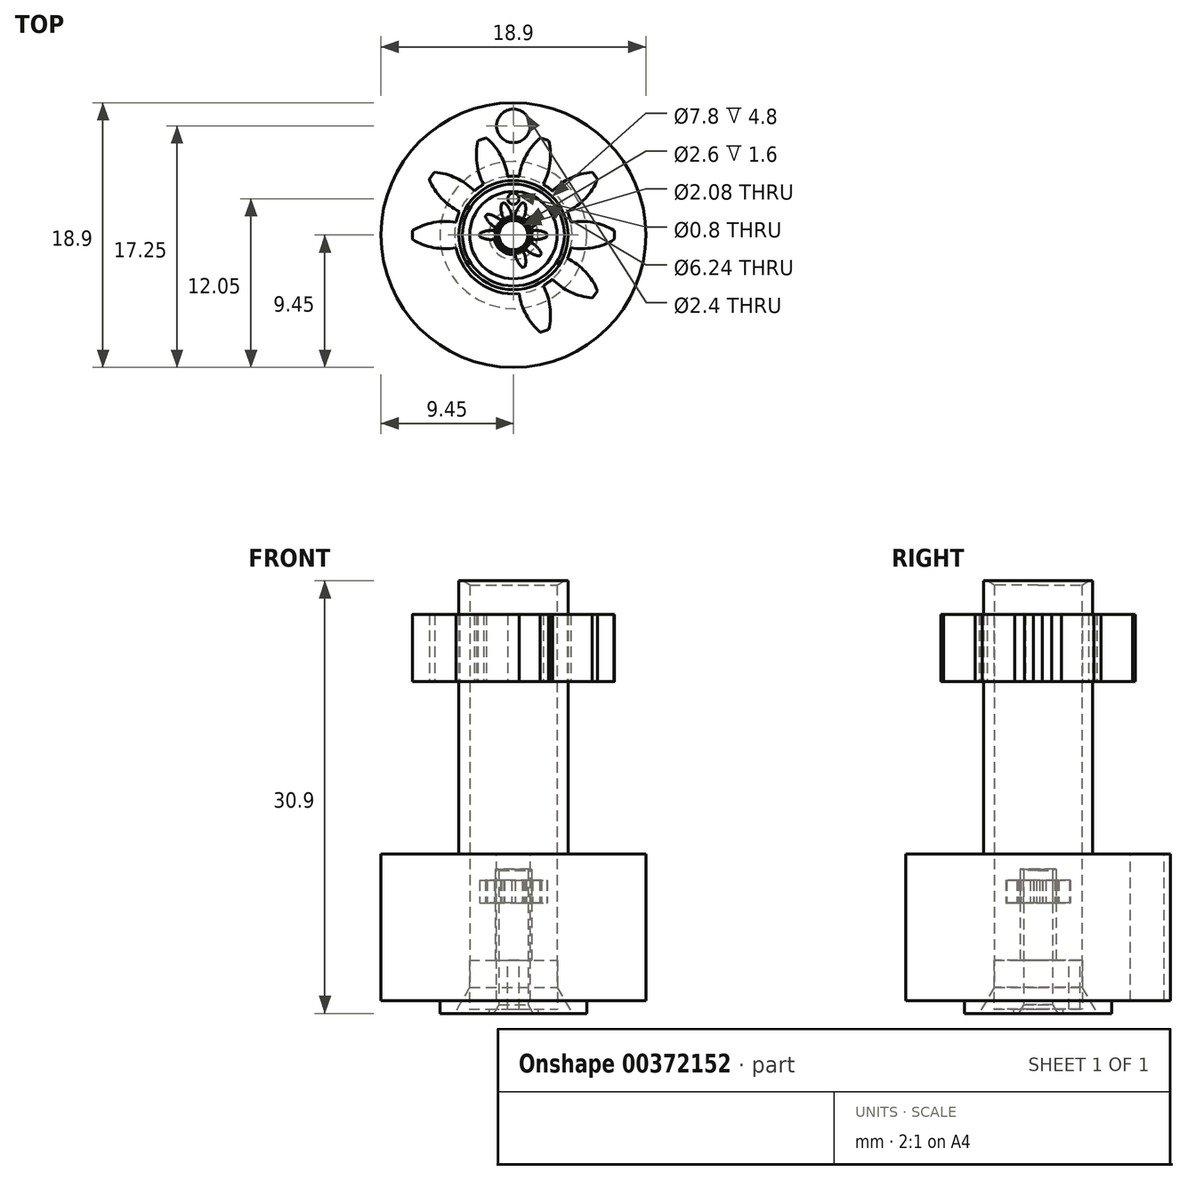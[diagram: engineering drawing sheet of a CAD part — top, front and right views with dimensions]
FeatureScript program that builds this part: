
annotation { "Feature Type Name" : "Feature", "Feature Type Description" : "" }
export const myFeature = defineFeature(function(context is Context, id is Id, definition is map)
    precondition{}
    {
        {
            var Q0;
            Q0=qCreatedBy(makeId("Front.planeOp"),FACE);
            var sketch = newSketch(context, id + "F0", { "sketchPlane" : qUnion([Q0])});
            skLineSegment(sketch, "E0", {"start": v(1.4, 0) * mm, "end": v(1.75, 0) * mm});
            skLineSegment(sketch, "E1", {"start": v(1.75, 0) * mm, "end": v(1.75, 0.3) * mm});
            skLineSegment(sketch, "E2", {"start": v(1.75, 0.3) * mm, "end": v(3.15, 0.3) * mm});
            skLineSegment(sketch, "E3", {"start": v(3.15, 0.3) * mm, "end": v(3.15, 3.8) * mm});
            skLineSegment(sketch, "E4", {"start": v(3.15, 3.8) * mm, "end": v(1.3, 3.8) * mm});
            skLineSegment(sketch, "E5", {"start": v(1.3, 3.8) * mm, "end": v(1.3, 10.3) * mm});
            skLineSegment(sketch, "E6", {"start": v(1.3, 10.3) * mm, "end": v(1.04, 10.3) * mm});
            skLineSegment(sketch, "E7", {"start": v(1.04, 10.3) * mm, "end": v(1.04, 0.62) * mm});
            skLineSegment(sketch, "E8", {"start": v(1.04, 0.62) * mm, "end": v(1.4, 0) * mm});
            skLineSegment(sketch, "E9", {"start": v(0, 0) * mm, "end": v(0, 10.3) * mm, "construction": true});
            skSolve(sketch);
        }
        {
            var Q0;
            Q0=makeQuery(id+"F0.imprint","IMPRINT",FACE,{"disambiguationData":[TD([[makeQuery(id+"F0.imprint","IMPRINT",EDGE,{"derivedFrom":sQuery(id+"F0.wireOp",EDGE,"E0")}),1.0]])]});
            var Q1;
            Q1=sQuery(id+"F0.wireOp",EDGE,"E9");
            revolve(context, id + "F1", {"entities" : qUnion([Q0]), "axis" : qUnion([Q1]), "revolveType" : RevolveType.FULL});
        }
        {
            var Q0;
            Q0=makeQuery(id+"F1.opRevolve","SWEPT_FACE",FACE,{"disambiguationData":[OSD([sQuery(id+"F0.wireOp",EDGE,"E6")])]});
            cPlane(context, id + "F2", {"entities" : qUnion([Q0]), "cplaneType" : CPlaneType.OFFSET, "offset" : 4.15 * mm, "oppositeDirection" : true, "width" : 150 * mm, "height" : 150 * mm});
        }
        {
            var Q0;
            Q0=qCreatedBy(id+"F2.planeOp",FACE);
            var sketch = newSketch(context, id + "F3", { "sketchPlane" : qUnion([Q0])});
            skCircle(sketch, "E10", {"center": v(0, 0) * mm, "radius": 2 * mm, "construction": true});
            skArc(sketch, "E11", {"start": v(-2.4, 0.1) * mm, "mid": v(-2.4, 0) * mm, "end": v(-2.4, -0.1) * mm});
            skCircle(sketch, "E12", {"center": v(0, 0) * mm, "radius": 1.4 * mm});
            skLineSegment(sketch, "E13", {"start": v(0, 0) * mm, "end": v(-1.94, -1.41) * mm, "construction": true});
            skArc(sketch, "E14", {"start": v(-1.37, 0.3) * mm, "mid": v(-1.9, 0.3) * mm, "end": v(-2.4, 0.1) * mm});
            skLineSegment(sketch, "E15", {"start": v(0, 0) * mm, "end": v(-1.94, 1.41) * mm, "construction": true});
            skArc(sketch, "E16", {"start": v(-2.4, -0.1) * mm, "mid": v(-1.9, -0.3) * mm, "end": v(-1.37, -0.3) * mm});
            skArc(sketch, "E17.1.0", {"start": v(-1.28, -0.56) * mm, "mid": v(-1.71, -0.88) * mm, "end": v(-2, -1.32) * mm});
            skArc(sketch, "E17.1.1", {"start": v(-1.88, -1.5) * mm, "mid": v(-1.36, -1.36) * mm, "end": v(-0.93, -1.05) * mm});
            skArc(sketch, "E17.1.2", {"start": v(-2, -1.32) * mm, "mid": v(-1.94, -1.41) * mm, "end": v(-1.88, -1.5) * mm});
            skArc(sketch, "E17.2.0", {"start": v(-0.71, -1.2) * mm, "mid": v(-0.87, -1.72) * mm, "end": v(-0.84, -2.25) * mm});
            skArc(sketch, "E17.2.1", {"start": v(-0.64, -2.31) * mm, "mid": v(-0.3, -1.9) * mm, "end": v(-0.13, -1.4) * mm});
            skArc(sketch, "E17.2.2", {"start": v(-0.84, -2.25) * mm, "mid": v(-0.74, -2.28) * mm, "end": v(-0.64, -2.31) * mm});
            skArc(sketch, "E17.3.0", {"start": v(0.13, -1.4) * mm, "mid": v(0.3, -1.9) * mm, "end": v(0.64, -2.31) * mm});
            skArc(sketch, "E17.3.1", {"start": v(0.84, -2.25) * mm, "mid": v(0.87, -1.72) * mm, "end": v(0.71, -1.2) * mm});
            skArc(sketch, "E17.3.2", {"start": v(0.64, -2.31) * mm, "mid": v(0.74, -2.28) * mm, "end": v(0.84, -2.25) * mm});
            skArc(sketch, "E17.4.0", {"start": v(0.93, -1.05) * mm, "mid": v(1.36, -1.36) * mm, "end": v(1.88, -1.5) * mm});
            skArc(sketch, "E17.4.1", {"start": v(2, -1.32) * mm, "mid": v(1.71, -0.88) * mm, "end": v(1.28, -0.56) * mm});
            skArc(sketch, "E17.4.2", {"start": v(1.88, -1.5) * mm, "mid": v(1.94, -1.41) * mm, "end": v(2, -1.32) * mm});
            skArc(sketch, "E17.5.0", {"start": v(1.37, -0.3) * mm, "mid": v(1.9, -0.3) * mm, "end": v(2.4, -0.1) * mm});
            skArc(sketch, "E17.5.1", {"start": v(2.4, 0.1) * mm, "mid": v(1.9, 0.3) * mm, "end": v(1.37, 0.3) * mm});
            skArc(sketch, "E17.5.2", {"start": v(2.4, -0.1) * mm, "mid": v(2.4, 0) * mm, "end": v(2.4, 0.1) * mm});
            skArc(sketch, "E17.6.0", {"start": v(1.28, 0.56) * mm, "mid": v(1.71, 0.88) * mm, "end": v(2, 1.32) * mm});
            skArc(sketch, "E17.6.1", {"start": v(1.88, 1.5) * mm, "mid": v(1.36, 1.36) * mm, "end": v(0.93, 1.05) * mm});
            skArc(sketch, "E17.6.2", {"start": v(2, 1.32) * mm, "mid": v(1.94, 1.41) * mm, "end": v(1.88, 1.5) * mm});
            skArc(sketch, "E17.7.0", {"start": v(0.71, 1.2) * mm, "mid": v(0.87, 1.72) * mm, "end": v(0.84, 2.25) * mm});
            skArc(sketch, "E17.7.1", {"start": v(0.64, 2.31) * mm, "mid": v(0.3, 1.9) * mm, "end": v(0.13, 1.4) * mm});
            skArc(sketch, "E17.7.2", {"start": v(0.84, 2.25) * mm, "mid": v(0.74, 2.28) * mm, "end": v(0.64, 2.31) * mm});
            skArc(sketch, "E17.8.0", {"start": v(-0.13, 1.4) * mm, "mid": v(-0.3, 1.9) * mm, "end": v(-0.64, 2.31) * mm});
            skArc(sketch, "E17.8.1", {"start": v(-0.84, 2.25) * mm, "mid": v(-0.87, 1.72) * mm, "end": v(-0.71, 1.2) * mm});
            skArc(sketch, "E17.8.2", {"start": v(-0.64, 2.31) * mm, "mid": v(-0.74, 2.28) * mm, "end": v(-0.84, 2.25) * mm});
            skArc(sketch, "E17.9.0", {"start": v(-0.93, 1.05) * mm, "mid": v(-1.36, 1.36) * mm, "end": v(-1.88, 1.5) * mm});
            skArc(sketch, "E17.9.1", {"start": v(-2, 1.32) * mm, "mid": v(-1.71, 0.88) * mm, "end": v(-1.28, 0.56) * mm});
            skArc(sketch, "E17.9.2", {"start": v(-1.88, 1.5) * mm, "mid": v(-1.94, 1.41) * mm, "end": v(-2, 1.32) * mm});
            skCircle(sketch, "E18", {"center": v(0, 0) * mm, "radius": 1.3 * mm});
            skSolve(sketch);
        }
        {
            var Q0;
            {var subQ6=sQuery(id+"F3.wireOp",EDGE,"E17.6.0");var subQ12=sQuery(id+"F3.wireOp",EDGE,"E17.7.0");var subQ17=sQuery(id+"F3.wireOp",EDGE,"E17.8.0");var subQ21=sQuery(id+"F3.wireOp",EDGE,"E17.9.0");var subQ27=sQuery(id+"F3.wireOp",EDGE,"E17.1.0");var subQ32=sQuery(id+"F3.wireOp",EDGE,"E17.2.0");var subQ37=sQuery(id+"F3.wireOp",EDGE,"E17.3.0");var subQ42=sQuery(id+"F3.wireOp",EDGE,"E17.4.0");var subQ47=sQuery(id+"F3.wireOp",EDGE,"E17.5.0");Q0=qUnion([makeQuery(id+"F3.imprint","IMPRINT",FACE,{"disambiguationData":[TD([[makeQuery(id+"F3.imprint","IMPRINT",EDGE,{"derivedFrom":sQuery(id+"F3.wireOp",EDGE,"E11")}),1.0]])]}),makeQuery(id+"F3.imprint","IMPRINT",FACE,{"disambiguationData":[TD([[makeQuery(id+"F3.imprint","IMPRINT",EDGE,{"derivedFrom":subQ6}),1.0]])]}),makeQuery(id+"F3.imprint","IMPRINT",FACE,{"disambiguationData":[TD([[makeQuery(id+"F3.imprint","IMPRINT",EDGE,{"derivedFrom":subQ12}),1.0]])]}),makeQuery(id+"F3.imprint","IMPRINT",FACE,{"disambiguationData":[TD([[makeQuery(id+"F3.imprint","IMPRINT",EDGE,{"derivedFrom":subQ17}),1.0]])]}),makeQuery(id+"F3.imprint","IMPRINT",FACE,{"disambiguationData":[TD([[makeQuery(id+"F3.imprint","IMPRINT",EDGE,{"derivedFrom":subQ21}),1.0]])]}),makeQuery(id+"F3.imprint","IMPRINT",FACE,{"disambiguationData":[TD([[makeQuery(id+"F3.imprint","IMPRINT",EDGE,{"derivedFrom":subQ27}),1.0]])]}),makeQuery(id+"F3.imprint","IMPRINT",FACE,{"disambiguationData":[TD([[makeQuery(id+"F3.imprint","IMPRINT",EDGE,{"derivedFrom":subQ32}),1.0]])]}),makeQuery(id+"F3.imprint","IMPRINT",FACE,{"disambiguationData":[TD([[makeQuery(id+"F3.imprint","IMPRINT",EDGE,{"derivedFrom":subQ37}),1.0]])]}),makeQuery(id+"F3.imprint","IMPRINT",FACE,{"disambiguationData":[TD([[makeQuery(id+"F3.imprint","IMPRINT",EDGE,{"derivedFrom":subQ42}),1.0]])]}),makeQuery(id+"F3.imprint","IMPRINT",FACE,{"disambiguationData":[TD([[makeQuery(id+"F3.imprint","IMPRINT",EDGE,{"derivedFrom":subQ47}),1.0]])]}),makeQuery(id+"F3.imprint","IMPRINT",FACE,{"disambiguationData":[TD([[makeQuery(id+"F3.imprint","IMPRINT",EDGE,{"derivedFrom":sQuery(id+"F3.wireOp",EDGE,"E18")}),-1.0]])]})]);}
            extrude(context, id + "F4", {"entities" : qUnion([Q0]), "depth" : 3.35 * mm});
        }
        {
            var Q0;
            Q0=makeQuery(id+"F1.opRevolve","SWEPT_FACE",FACE,{"disambiguationData":[OSD([sQuery(id+"F0.wireOp",EDGE,"E4")])]});
            var sketch = newSketch(context, id + "F5", { "sketchPlane" : qUnion([Q0])});
            skCircle(sketch, "E19", {"center": v(0, 2.6) * mm, "radius": 0.4 * mm});
            skSolve(sketch);
        }
        {
            var Q0;
            Q0=makeQuery(id+"F5.imprint","IMPRINT",FACE,{"disambiguationData":[TD([[makeQuery(id+"F5.imprint","IMPRINT",EDGE,{"derivedFrom":sQuery(id+"F5.wireOp",EDGE,"E19")}),1.0]])]});
            extrude(context, id + "F6", {"entities" : qUnion([Q0]), "operationType" : NewBodyOperationType.REMOVE, "endBound" : BoundingType.THROUGH_ALL, "oppositeDirection" : true, "depth" : 25 * mm});
        }
        {
            var Q0;
            Q0=makeQuery(id+"F1.opRevolve","SWEPT_BODY",BODY,{"disambiguationData":[OSD([sQuery(id+"F0.wireOp",EDGE,"E0"),sQuery(id+"F0.wireOp",EDGE,"E1"),sQuery(id+"F0.wireOp",EDGE,"E2"),sQuery(id+"F0.wireOp",EDGE,"E3"),sQuery(id+"F0.wireOp",EDGE,"E4"),sQuery(id+"F0.wireOp",EDGE,"E5"),sQuery(id+"F0.wireOp",EDGE,"E6"),sQuery(id+"F0.wireOp",EDGE,"E7"),sQuery(id+"F0.wireOp",EDGE,"E8")])]});
            var Q1;
            Q1=makeQuery(id+"F4.opExtrude","SWEPT_BODY",BODY,{"disambiguationData":[OSD([sQuery(id+"F3.wireOp",EDGE,"E11"),sQuery(id+"F3.wireOp",EDGE,"E12"),sQuery(id+"F3.wireOp",EDGE,"E14"),sQuery(id+"F3.wireOp",EDGE,"E16"),sQuery(id+"F3.wireOp",EDGE,"E17.1.0"),sQuery(id+"F3.wireOp",EDGE,"E17.1.1"),sQuery(id+"F3.wireOp",EDGE,"E17.1.2"),sQuery(id+"F3.wireOp",EDGE,"E17.2.0"),sQuery(id+"F3.wireOp",EDGE,"E17.2.1"),sQuery(id+"F3.wireOp",EDGE,"E17.2.2"),sQuery(id+"F3.wireOp",EDGE,"E17.3.0"),sQuery(id+"F3.wireOp",EDGE,"E17.3.1"),sQuery(id+"F3.wireOp",EDGE,"E17.3.2"),sQuery(id+"F3.wireOp",EDGE,"E17.4.0"),sQuery(id+"F3.wireOp",EDGE,"E17.4.1"),sQuery(id+"F3.wireOp",EDGE,"E17.4.2"),sQuery(id+"F3.wireOp",EDGE,"E17.5.0"),sQuery(id+"F3.wireOp",EDGE,"E17.5.1"),sQuery(id+"F3.wireOp",EDGE,"E17.5.2"),sQuery(id+"F3.wireOp",EDGE,"E17.6.0"),sQuery(id+"F3.wireOp",EDGE,"E17.6.1"),sQuery(id+"F3.wireOp",EDGE,"E17.6.2"),sQuery(id+"F3.wireOp",EDGE,"E17.7.0"),sQuery(id+"F3.wireOp",EDGE,"E17.7.1"),sQuery(id+"F3.wireOp",EDGE,"E17.7.2"),sQuery(id+"F3.wireOp",EDGE,"E17.8.0"),sQuery(id+"F3.wireOp",EDGE,"E17.8.1"),sQuery(id+"F3.wireOp",EDGE,"E17.8.2"),sQuery(id+"F3.wireOp",EDGE,"E17.9.0"),sQuery(id+"F3.wireOp",EDGE,"E17.9.1"),sQuery(id+"F3.wireOp",EDGE,"E17.9.2"),sQuery(id+"F3.wireOp",EDGE,"E18")])]});
            transform(context, id + "F7", {"entities" : qUnion([Q0, Q1]), "transformType" : TransformType.COPY});
        }
        {
            var Q0;
            Q0=makeQuery(id+"F7.opPattern","COPY",BODY,{"derivedFrom":makeQuery(id+"F1.opRevolve","SWEPT_BODY",BODY,{"disambiguationData":[OSD([sQuery(id+"F0.wireOp",EDGE,"E0"),sQuery(id+"F0.wireOp",EDGE,"E1"),sQuery(id+"F0.wireOp",EDGE,"E2"),sQuery(id+"F0.wireOp",EDGE,"E3"),sQuery(id+"F0.wireOp",EDGE,"E4"),sQuery(id+"F0.wireOp",EDGE,"E5"),sQuery(id+"F0.wireOp",EDGE,"E6"),sQuery(id+"F0.wireOp",EDGE,"E7"),sQuery(id+"F0.wireOp",EDGE,"E8")])]}),"instanceName":"1"});
            deleteBodies(context, id + "F8", {"entities" : qUnion([Q0])});
        }
        {
            var Q0;
            Q0=makeQuery(id+"F1.opRevolve","SWEPT_EDGE",EDGE,{"disambiguationData":[OSD([sQuery(id+"F0.wireOp",EDGE,"E6"),sQuery(id+"F0.wireOp",EDGE,"E7")])]});
            chamfer(context, id + "F9", {"entities" : qUnion([Q0]), "chamferType" : ChamferType.OFFSET_ANGLE, "width" : 0.1 * mm, "oppositeDirection" : true, "angle" : 60 * degree, "tangentPropagation" : true});
        }
        {
            var Q0;
            Q0=qCreatedBy(makeId("Front.planeOp"),FACE);
            var sketch = newSketch(context, id + "F10", { "sketchPlane" : qUnion([Q0])});
            skLineSegment(sketch, "E20", {"start": v(0, 0) * mm, "end": v(0, 10.3) * mm, "construction": true});
            skLineSegment(sketch, "E21.bottom", {"start": v(1.3, 7.9) * mm, "end": v(2.4, 7.9) * mm});
            skLineSegment(sketch, "E21.top", {"start": v(1.3, 6.8) * mm, "end": v(2.4, 6.8) * mm});
            skLineSegment(sketch, "E21.left", {"start": v(1.3, 7.9) * mm, "end": v(1.3, 6.8) * mm});
            skLineSegment(sketch, "E21.right", {"start": v(2.4, 7.9) * mm, "end": v(2.4, 6.8) * mm});
            skSolve(sketch);
        }
        {
            var Q0;
            Q0=makeQuery(id+"F10.imprint","IMPRINT",FACE,{"disambiguationData":[TD([[makeQuery(id+"F10.imprint","IMPRINT",EDGE,{"derivedFrom":sQuery(id+"F10.wireOp",EDGE,"E21.bottom")}),-1.0]])]});
            var Q1;
            Q1=sQuery(id+"F10.wireOp",EDGE,"E20");
            revolve(context, id + "F11", {"operationType" : NewBodyOperationType.REMOVE, "entities" : qUnion([Q0]), "axis" : qUnion([Q1]), "revolveType" : RevolveType.FULL, "oppositeDirection" : true});
        }
        {
            var Q0;
            {var subQ1=sQuery(id+"F3.wireOp",EDGE,"E17.2.0");Q0=makeQuery(id+"F3.imprint","IMPRINT",FACE,{"disambiguationData":[TD([[makeQuery(id+"F3.imprint","IMPRINT",EDGE,{"derivedFrom":subQ1}),1.0]])]});}
            var Q1;
            {var subQ1=sQuery(id+"F3.wireOp",EDGE,"E17.1.0");Q1=makeQuery(id+"F3.imprint","IMPRINT",FACE,{"disambiguationData":[TD([[makeQuery(id+"F3.imprint","IMPRINT",EDGE,{"derivedFrom":subQ1}),1.0]])]});}
            extrude(context, id + "F12", {"entities" : qUnion([Q0, Q1]), "operationType" : NewBodyOperationType.REMOVE, "depth" : 25 * mm});
        }
        {
            var Q0;
            Q0=makeQuery(id+"F1.opRevolve","SWEPT_BODY",BODY,{"disambiguationData":[OSD([sQuery(id+"F0.wireOp",EDGE,"E0"),sQuery(id+"F0.wireOp",EDGE,"E1"),sQuery(id+"F0.wireOp",EDGE,"E2"),sQuery(id+"F0.wireOp",EDGE,"E3"),sQuery(id+"F0.wireOp",EDGE,"E4"),sQuery(id+"F0.wireOp",EDGE,"E5"),sQuery(id+"F0.wireOp",EDGE,"E6"),sQuery(id+"F0.wireOp",EDGE,"E7"),sQuery(id+"F0.wireOp",EDGE,"E8")])]});
            transform(context, id + "F13", {"entities" : qUnion([Q0]), "transformType" : TransformType.TRANSLATION_3D, "dx" : 0 * mm, "dy" : 0 * mm, "dz" : 0 * mm, "makeCopy" : true});
        }
        {
            var Q0;
            Q0=makeQuery(id+"F7.opPattern","COPY",FACE,{"derivedFrom":makeQuery(id+"F4.opExtrude","CAP_FACE",FACE,{"disambiguationData":[OSD([sQuery(id+"F3.wireOp",EDGE,"E11"),sQuery(id+"F3.wireOp",EDGE,"E12"),sQuery(id+"F3.wireOp",EDGE,"E14"),sQuery(id+"F3.wireOp",EDGE,"E16"),sQuery(id+"F3.wireOp",EDGE,"E17.1.0"),sQuery(id+"F3.wireOp",EDGE,"E17.1.1"),sQuery(id+"F3.wireOp",EDGE,"E17.1.2"),sQuery(id+"F3.wireOp",EDGE,"E17.2.0"),sQuery(id+"F3.wireOp",EDGE,"E17.2.1"),sQuery(id+"F3.wireOp",EDGE,"E17.2.2"),sQuery(id+"F3.wireOp",EDGE,"E17.3.0"),sQuery(id+"F3.wireOp",EDGE,"E17.3.1"),sQuery(id+"F3.wireOp",EDGE,"E17.3.2"),sQuery(id+"F3.wireOp",EDGE,"E17.4.0"),sQuery(id+"F3.wireOp",EDGE,"E17.4.1"),sQuery(id+"F3.wireOp",EDGE,"E17.4.2"),sQuery(id+"F3.wireOp",EDGE,"E17.5.0"),sQuery(id+"F3.wireOp",EDGE,"E17.5.1"),sQuery(id+"F3.wireOp",EDGE,"E17.5.2"),sQuery(id+"F3.wireOp",EDGE,"E17.6.0"),sQuery(id+"F3.wireOp",EDGE,"E17.6.1"),sQuery(id+"F3.wireOp",EDGE,"E17.6.2"),sQuery(id+"F3.wireOp",EDGE,"E17.7.0"),sQuery(id+"F3.wireOp",EDGE,"E17.7.1"),sQuery(id+"F3.wireOp",EDGE,"E17.7.2"),sQuery(id+"F3.wireOp",EDGE,"E17.8.0"),sQuery(id+"F3.wireOp",EDGE,"E17.8.1"),sQuery(id+"F3.wireOp",EDGE,"E17.8.2"),sQuery(id+"F3.wireOp",EDGE,"E17.9.0"),sQuery(id+"F3.wireOp",EDGE,"E17.9.1"),sQuery(id+"F3.wireOp",EDGE,"E17.9.2"),sQuery(id+"F3.wireOp",EDGE,"E18")])],"isStart":true}),"instanceName":"1"});
            extrude(context, id + "F14", {"entities" : qUnion([Q0]), "operationType" : NewBodyOperationType.REMOVE, "oppositeDirection" : true, "depth" : 0.85 * mm});
        }
        {
            var Q0;
            {var subQ1=sQuery(id+"F3.wireOp",EDGE,"E17.2.0");Q0=makeQuery(id+"F3.imprint","IMPRINT",FACE,{"disambiguationData":[TD([[makeQuery(id+"F3.imprint","IMPRINT",EDGE,{"derivedFrom":subQ1}),1.0]])]});}
            var Q1;
            {var subQ1=sQuery(id+"F3.wireOp",EDGE,"E17.1.0");Q1=makeQuery(id+"F3.imprint","IMPRINT",FACE,{"disambiguationData":[TD([[makeQuery(id+"F3.imprint","IMPRINT",EDGE,{"derivedFrom":subQ1}),1.0]])]});}
            extrude(context, id + "F15", {"entities" : qUnion([Q0, Q1]), "operationType" : NewBodyOperationType.REMOVE, "depth" : 1.75 * mm});
        }
        {
            var Q0;
            Q0=makeQuery(id+"F1.opRevolve","SWEPT_BODY",BODY,{"disambiguationData":[OSD([sQuery(id+"F0.wireOp",EDGE,"E0"),sQuery(id+"F0.wireOp",EDGE,"E1"),sQuery(id+"F0.wireOp",EDGE,"E2"),sQuery(id+"F0.wireOp",EDGE,"E3"),sQuery(id+"F0.wireOp",EDGE,"E4"),sQuery(id+"F0.wireOp",EDGE,"E5"),sQuery(id+"F0.wireOp",EDGE,"E6"),sQuery(id+"F0.wireOp",EDGE,"E7"),sQuery(id+"F0.wireOp",EDGE,"E8")])]});
            var Q1;
            Q1=makeQuery(id+"F7.opPattern","COPY",BODY,{"derivedFrom":makeQuery(id+"F4.opExtrude","SWEPT_BODY",BODY,{"disambiguationData":[OSD([sQuery(id+"F3.wireOp",EDGE,"E11"),sQuery(id+"F3.wireOp",EDGE,"E12"),sQuery(id+"F3.wireOp",EDGE,"E14"),sQuery(id+"F3.wireOp",EDGE,"E16"),sQuery(id+"F3.wireOp",EDGE,"E17.1.0"),sQuery(id+"F3.wireOp",EDGE,"E17.1.1"),sQuery(id+"F3.wireOp",EDGE,"E17.1.2"),sQuery(id+"F3.wireOp",EDGE,"E17.2.0"),sQuery(id+"F3.wireOp",EDGE,"E17.2.1"),sQuery(id+"F3.wireOp",EDGE,"E17.2.2"),sQuery(id+"F3.wireOp",EDGE,"E17.3.0"),sQuery(id+"F3.wireOp",EDGE,"E17.3.1"),sQuery(id+"F3.wireOp",EDGE,"E17.3.2"),sQuery(id+"F3.wireOp",EDGE,"E17.4.0"),sQuery(id+"F3.wireOp",EDGE,"E17.4.1"),sQuery(id+"F3.wireOp",EDGE,"E17.4.2"),sQuery(id+"F3.wireOp",EDGE,"E17.5.0"),sQuery(id+"F3.wireOp",EDGE,"E17.5.1"),sQuery(id+"F3.wireOp",EDGE,"E17.5.2"),sQuery(id+"F3.wireOp",EDGE,"E17.6.0"),sQuery(id+"F3.wireOp",EDGE,"E17.6.1"),sQuery(id+"F3.wireOp",EDGE,"E17.6.2"),sQuery(id+"F3.wireOp",EDGE,"E17.7.0"),sQuery(id+"F3.wireOp",EDGE,"E17.7.1"),sQuery(id+"F3.wireOp",EDGE,"E17.7.2"),sQuery(id+"F3.wireOp",EDGE,"E17.8.0"),sQuery(id+"F3.wireOp",EDGE,"E17.8.1"),sQuery(id+"F3.wireOp",EDGE,"E17.8.2"),sQuery(id+"F3.wireOp",EDGE,"E17.9.0"),sQuery(id+"F3.wireOp",EDGE,"E17.9.1"),sQuery(id+"F3.wireOp",EDGE,"E17.9.2"),sQuery(id+"F3.wireOp",EDGE,"E18")])]}),"instanceName":"1"});
            var Q2;
            Q2=qCreatedBy(makeId("Origin.pointOp"),VERTEX);
            transform(context, id + "F16", {"entities" : qUnion([Q0, Q1]), "transformType" : TransformType.SCALE_UNIFORMLY, "scale" : 3, "makeCopy" : false, "scalePoint" : qUnion([Q2])});
        }
    });
